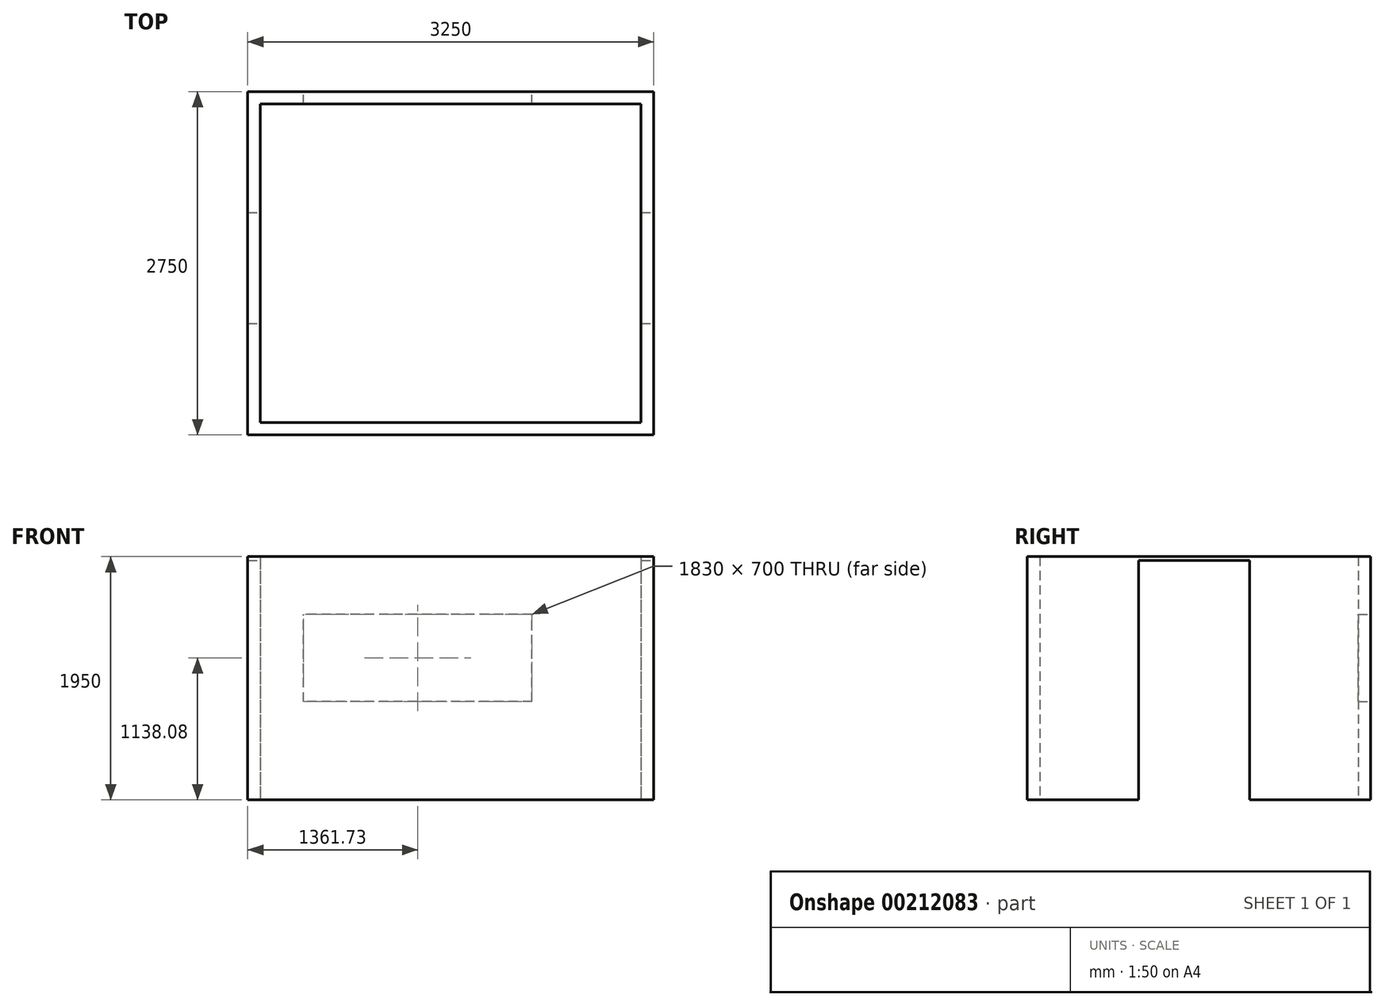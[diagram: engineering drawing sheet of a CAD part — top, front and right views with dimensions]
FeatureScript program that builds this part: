
annotation { "Feature Type Name" : "Feature", "Feature Type Description" : "" }
export const myFeature = defineFeature(function(context is Context, id is Id, definition is map)
    precondition{}
    {
        {
            var Q0;
            Q0=qCreatedBy(makeId("Top.planeOp"),FACE);
            var sketch = newSketch(context, id + "F0", { "sketchPlane" : qUnion([Q0])});
            skLineSegment(sketch, "E0.bottom", {"start": v(-50.05, -46.38) * mm, "end": v(3199.95, -46.38) * mm});
            skLineSegment(sketch, "E0.top", {"start": v(-50.05, 2703.62) * mm, "end": v(3199.95, 2703.62) * mm});
            skLineSegment(sketch, "E0.left", {"start": v(-50.05, -46.38) * mm, "end": v(-50.05, 2703.62) * mm});
            skLineSegment(sketch, "E0.right", {"start": v(3199.95, -46.38) * mm, "end": v(3199.95, 2703.62) * mm});
            skSolve(sketch);
        }
        {
            var Q0;
            Q0=makeQuery(id+"F0.imprint","IMPRINT",FACE,{"disambiguationData":[TD([[makeQuery(id+"F0.imprint","IMPRINT",EDGE,{"derivedFrom":sQuery(id+"F0.wireOp",EDGE,"E0.bottom")}),1.0]])]});
            extrude(context, id + "F1", {"entities" : qUnion([Q0]), "depth" : 1950 * mm});
        }
        {
            var Q0;
            Q0=makeQuery(id+"F1.opExtrude","CAP_FACE",FACE,{"disambiguationData":[OSD([sQuery(id+"F0.wireOp",EDGE,"E0.bottom"),sQuery(id+"F0.wireOp",EDGE,"E0.top"),sQuery(id+"F0.wireOp",EDGE,"E0.left"),sQuery(id+"F0.wireOp",EDGE,"E0.right")])],"isStart":false});
            var Q1;
            Q1=makeQuery(id+"F1.opExtrude","SWEPT_BODY",BODY,{"disambiguationData":[OSD([sQuery(id+"F0.wireOp",EDGE,"E0.bottom"),sQuery(id+"F0.wireOp",EDGE,"E0.top"),sQuery(id+"F0.wireOp",EDGE,"E0.left"),sQuery(id+"F0.wireOp",EDGE,"E0.right")])]});
            shell(context, id + "F2", {"entities" : qUnion([Q0]), "parts" : qUnion([Q1]), "thickness" : 100 * mm});
        }
        {
            var Q0;
            Q0=makeQuery(id+"F2.opShell","OFFSET_FACE",FACE,{"disambiguationData":[OSD([sQuery(id+"F0.wireOp",EDGE,"E0.bottom"),sQuery(id+"F0.wireOp",EDGE,"E0.top"),sQuery(id+"F0.wireOp",EDGE,"E0.left"),sQuery(id+"F0.wireOp",EDGE,"E0.right")])]});
            extrude(context, id + "F3", {"entities" : qUnion([Q0]), "operationType" : NewBodyOperationType.REMOVE, "oppositeDirection" : true, "depth" : 200 * mm});
        }
        {
            var Q0;
            Q0=makeQuery(id+"F1.opExtrude","SWEPT_FACE",FACE,{"disambiguationData":[OSD([sQuery(id+"F0.wireOp",EDGE,"E0.right")])]});
            var sketch = newSketch(context, id + "F4", { "sketchPlane" : qUnion([Q0])});
            skLineSegment(sketch, "E1.bottom", {"start": v(1734.67, 0) * mm, "end": v(844.67, 0) * mm});
            skLineSegment(sketch, "E1.top", {"start": v(1734.67, 1920) * mm, "end": v(844.67, 1920) * mm});
            skLineSegment(sketch, "E1.left", {"start": v(1734.67, 0) * mm, "end": v(1734.67, 1920) * mm});
            skLineSegment(sketch, "E1.right", {"start": v(844.67, 0) * mm, "end": v(844.67, 1920) * mm});
            skSolve(sketch);
        }
        {
            var Q0;
            Q0=makeQuery(id+"F4.imprint","IMPRINT",FACE,{"disambiguationData":[TD([[makeQuery(id+"F4.imprint","IMPRINT",EDGE,{"derivedFrom":sQuery(id+"F4.wireOp",EDGE,"E1.bottom")}),1.0]])]});
            extrude(context, id + "F5", {"entities" : qUnion([Q0]), "operationType" : NewBodyOperationType.REMOVE, "oppositeDirection" : true, "depth" : 4000 * mm});
        }
        {
            var Q0;
            Q0=makeQuery(id+"F1.opExtrude","SWEPT_FACE",FACE,{"disambiguationData":[OSD([sQuery(id+"F0.wireOp",EDGE,"E0.top")])]});
            var sketch = newSketch(context, id + "F6", { "sketchPlane" : qUnion([Q0])});
            skSolve(sketch);
        }
        {
            var Q0;
            {var subQ0=sQuery(id+"F0.wireOp",EDGE,"E0.top");Q0=makeQuery(id+"F6.imprint","IMPRINT",FACE,{"disambiguationData":[TD([[makeQuery(id+"F6.imprint","IMPRINT",EDGE,{"derivedFrom":makeQuery(id+"F1.opExtrude","CAP_EDGE",EDGE,{"disambiguationData":[OSD([subQ0])],"isStart":true})}),-1.0]])]});}
            var sketch = newSketch(context, id + "F7", { "sketchPlane" : qUnion([Q0])});
            skLineSegment(sketch, "E2.bottom", {"start": v(-2226.68, 788.08) * mm, "end": v(-396.68, 788.08) * mm});
            skLineSegment(sketch, "E2.top", {"start": v(-2226.68, 1488.08) * mm, "end": v(-396.68, 1488.08) * mm});
            skLineSegment(sketch, "E2.left", {"start": v(-2226.68, 788.08) * mm, "end": v(-2226.68, 1488.08) * mm});
            skLineSegment(sketch, "E2.right", {"start": v(-396.68, 788.08) * mm, "end": v(-396.68, 1488.08) * mm});
            skSolve(sketch);
        }
        {
            var Q0;
            Q0=makeQuery(id+"F7.imprint","IMPRINT",FACE,{"disambiguationData":[TD([[makeQuery(id+"F7.imprint","IMPRINT",EDGE,{"derivedFrom":sQuery(id+"F7.wireOp",EDGE,"E2.bottom")}),1.0]])]});
            extrude(context, id + "F8", {"entities" : qUnion([Q0]), "operationType" : NewBodyOperationType.REMOVE, "oppositeDirection" : true, "depth" : 200 * mm});
        }
    });
